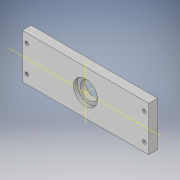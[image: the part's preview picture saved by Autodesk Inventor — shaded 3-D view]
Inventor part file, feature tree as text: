
AUTODESK INVENTOR PART (.ipt)
format: ipt  version: 2018 (Build 220112000, 112)  size: 125,952 bytes
history: native  units: mm
features: extrude x4, sketch x4, other x1
ambient origin geometry x8: Origin, YZ Plane, XZ Plane, XY Plane, X Axis, Y Axis, Z Axis, Center Point
bodies: Body1 (feature_tree)
feature tree (9):
  other  "ソリッド1"
  extrude  "押し出し1"  Depth=50.0mm
  extrude  "押し出し2"  Depth=142.0mm
  extrude  "押し出し3"  Depth=10.0mm TaperAngle=0.0deg
  extrude  "押し出し4"  Depth=27.0mm
  sketch  "スケッチ3"
  sketch  "スケッチ4"
  sketch  "スケッチ5"
  sketch  "スケッチ6"
